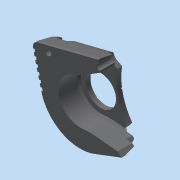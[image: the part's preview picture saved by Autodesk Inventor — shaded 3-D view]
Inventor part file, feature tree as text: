
AUTODESK INVENTOR PART (.ipt)
format: ipt  version: 2014 SP1 (Build 180222100, 222)  size: 320,000 bytes
history: native  units: in
note: dims shown in document units (in); Inventor stores cm internally (conversion verified against a paired STEP export)
features: sketch x9, other x3
ambient origin geometry x8: Origin, YZ Plane, XZ Plane, XY Plane, X Axis, Y Axis, Z Axis, Center Point
bodies: Solid1 (feature_tree)
feature tree (12):
  other  "pulleyprotector.ipt"
  other  "Solid1::pulleyprotector.ipt"
  other  "TaggingFeature1"
  sketch  "Sketch22"
  sketch  "Sketch2"  dims[d0=0.3937in]
  sketch  "Sketch6"  dims[d1=0.1181in d2=0.2362in d3=0.1772in d5=0.6693in d6=0.0in d31=1.6914in d32=3.5433in d42=0.315in d43=0.9843in d44=0.1575in d45=0.0in d46=0.1in d64=0.201in d65=0.201in d67=0.0in d68=0.425in d69=0.425in d70=0.1969in d71=0.0in d81=0.1181in d82=0.3543in d83=0.0in d98=0.1969in d115=0.5906in d116=0.0394in d117=150.0deg d118=0.0197in d119=0.0in d120=1.9685in d121=360.0deg d125=0.0591in d129=0.0in d130=0.1772in d131=0.1in d132=2.3622in d134=0.2in d139=0.05in d140=0.0in d144=0.17in d148=0.2in d151=0.2in]
  sketch  "Sketch9"
  sketch  "Sketch10"
  sketch  "Sketch12"
  sketch  "Sketch14"
  sketch  "Sketch18"
  sketch  "Sketch16"
